# Revit family: Soap_Dispenser-American_Standard-4503_Series
name_source: partatom
category: Specialty Equipment
revit_build: Autodesk Revit 2014 (Build: 20130308_1515(x64)
units: mm (PartAtom-declared; Revit-internal decimal feet)

## types (6) — shared parameters
Assembly Code = C1030
Default Elevation = 0"
Description = Liquid Soap Dispenser
Finish = Metal-American Standard-002-Polished Chrome
Height = 2 15/16"
Installation Type = Deck Mounted
Length = 3"
Manufacturer = American Standard
Material = Metal-American Standard-002-Polished Chrome
Price = Prices may vary. Please consult Manufacturer Representative for most up-to-date price list.
Product Documentation Link = https://www.americanstandard-us.com
Product Page URL = https://www.americanstandard-us.com
URL = https://www.americanstandard-us.com
Warranty Information = Limited Lifetime Function and Finish Warranty
Width = 1 3/16"

## type names (no varying parameters)
- 4503.120.002
- 4503.120.075
- 4503.120.013
- 4503.120.278
- 4503.120.224
- 4503.120.243

note: column(s) folded — value = type name in every type: Model

## geometry (parser evidence)
native form markers: Sweep x1
no freeform markers — native parametric forms only
